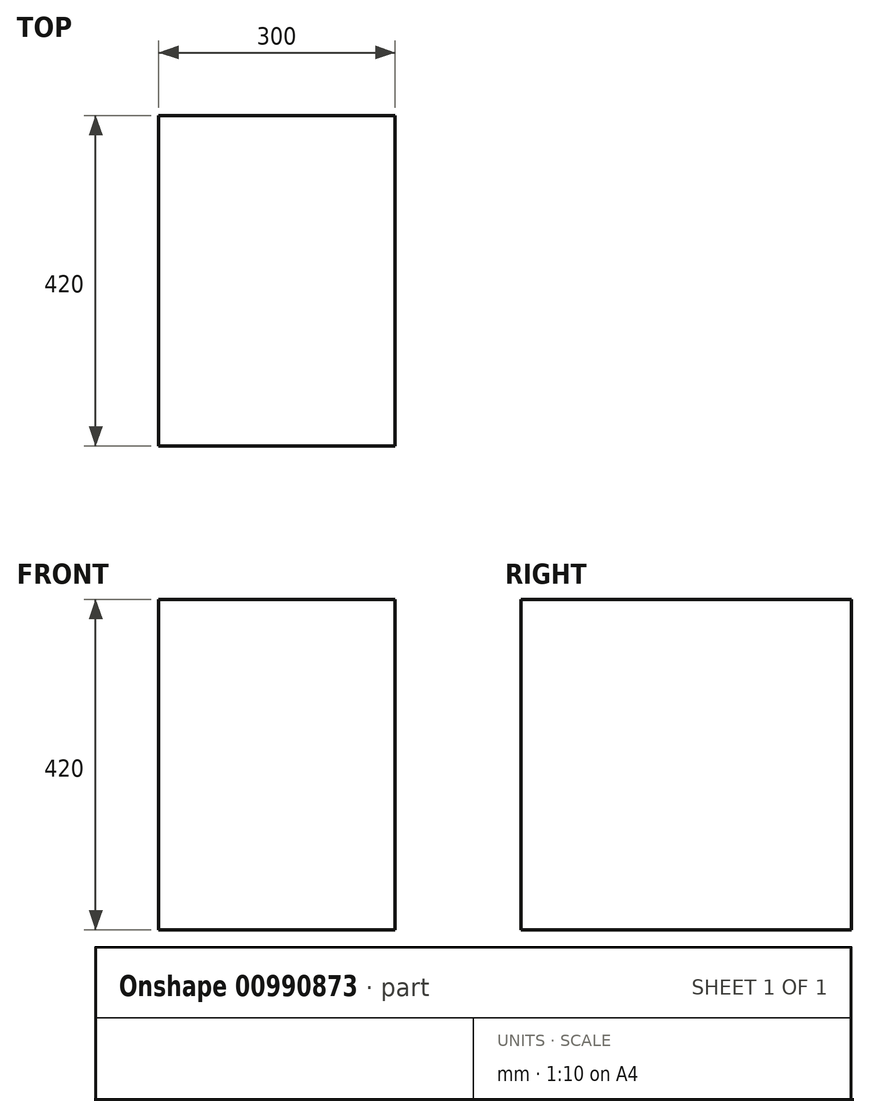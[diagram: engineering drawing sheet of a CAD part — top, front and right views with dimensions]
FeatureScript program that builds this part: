
annotation { "Feature Type Name" : "Feature", "Feature Type Description" : "" }
export const myFeature = defineFeature(function(context is Context, id is Id, definition is map)
    precondition{}
    {
        {
            var Q0;
            Q0=qCreatedBy(makeId("Top.planeOp"),FACE);
            var sketch = newSketch(context, id + "F0", { "sketchPlane" : qUnion([Q0])});
            skLineSegment(sketch, "E0.bottom", {"start": v(0, 0) * mm, "end": v(300, 0) * mm});
            skLineSegment(sketch, "E0.top", {"start": v(0, 420) * mm, "end": v(300, 420) * mm});
            skLineSegment(sketch, "E0.left", {"start": v(0, 0) * mm, "end": v(0, 420) * mm});
            skLineSegment(sketch, "E0.right", {"start": v(300, 0) * mm, "end": v(300, 420) * mm});
            skSolve(sketch);
        }
        {
            var Q0;
            Q0=makeQuery(id+"F0.imprint","IMPRINT",FACE,{"disambiguationData":[TD([[makeQuery(id+"F0.imprint","IMPRINT",EDGE,{"derivedFrom":sQuery(id+"F0.wireOp",EDGE,"E0.bottom")}),1.0]])]});
            extrude(context, id + "F1", {"entities" : qUnion([Q0]), "depth" : 420 * mm, "offsetDistance" : 25 * mm});
        }
    });
